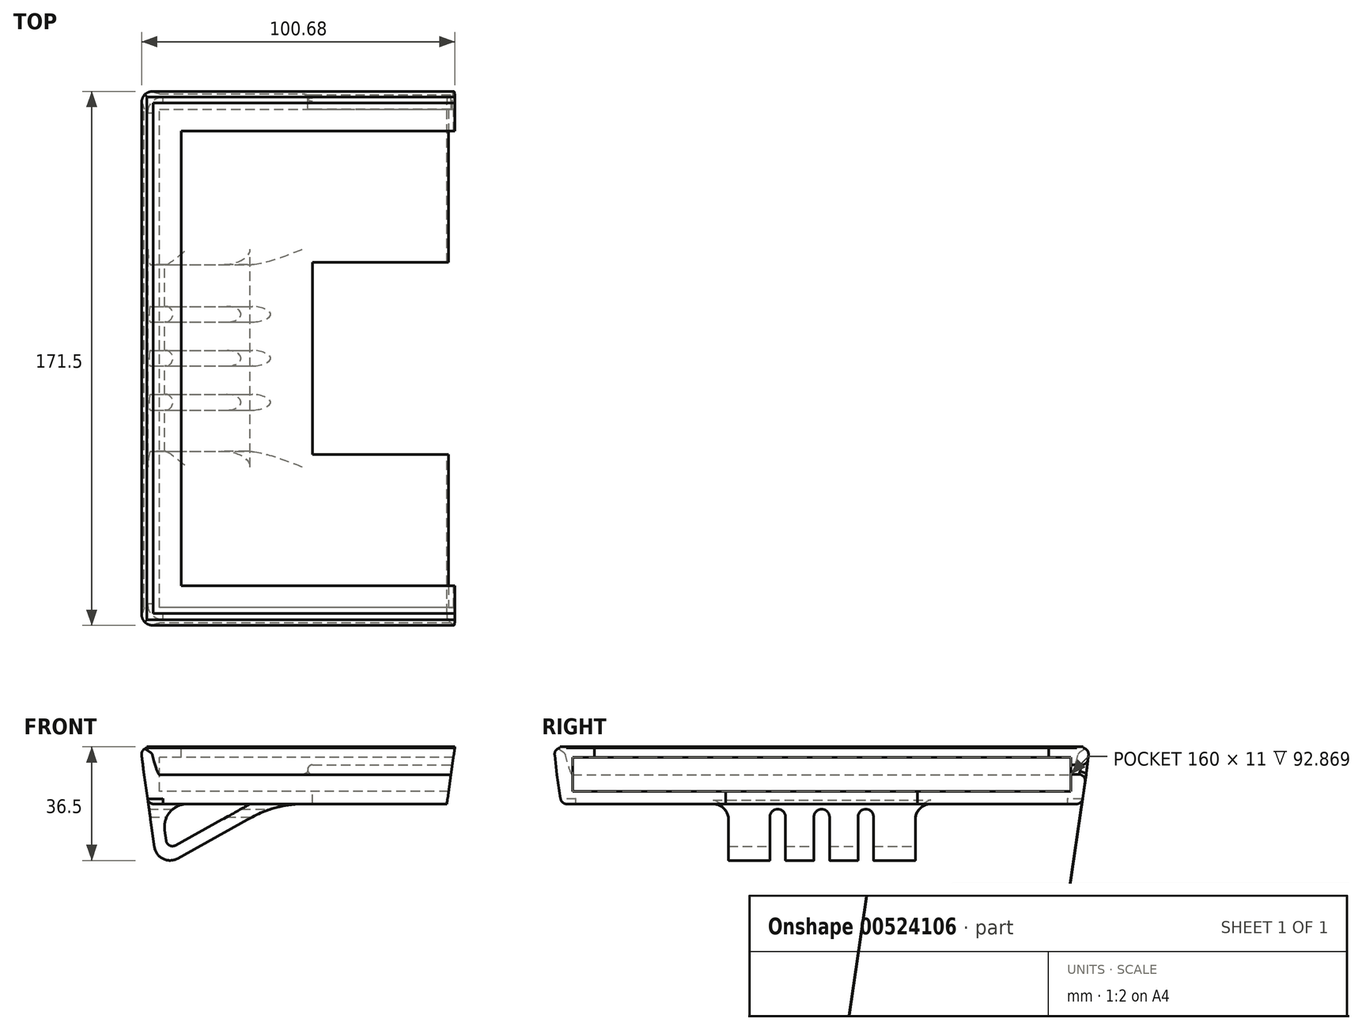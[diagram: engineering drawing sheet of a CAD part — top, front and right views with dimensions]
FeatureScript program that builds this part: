
annotation { "Feature Type Name" : "Feature", "Feature Type Description" : "" }
export const myFeature = defineFeature(function(context is Context, id is Id, definition is map)
    precondition{}
    {
        {
            var Q0;
            Q0=qCreatedBy(makeId("Right.planeOp"),FACE);
            var sketch = newSketch(context, id + "F0", { "sketchPlane" : qUnion([Q0])});
            skLineSegment(sketch, "E0.top", {"start": v(-5, -11) * mm, "end": v(44.17, -11) * mm});
            skLineSegment(sketch, "E0.right", {"start": v(44.17, -15) * mm, "end": v(44.17, -11) * mm});
            skLineSegment(sketch, "E1", {"start": v(2, 3) * mm, "end": v(2, 0) * mm});
            skLineSegment(sketch, "E2", {"start": v(2, 0) * mm, "end": v(-5, 0) * mm});
            skLineSegment(sketch, "E3", {"start": v(-5, 0) * mm, "end": v(-5, -11) * mm});
            skPoint(sketch, "E4.visualSharp", {"position": v(-11, 3) * mm});
            skPoint(sketch, "E5.visualSharp", {"position": v(-11, -15) * mm});
            skPoint(sketch, "E6.start.orphan", {"position": v(-9, -2) * mm});
            skPoint(sketch, "E7.end.orphan", {"position": v(-11, 1) * mm});
            skPoint(sketch, "E0.left.end.orphan", {"position": v(-11, -11) * mm});
            skPoint(sketch, "E5.filletArc.start.orphan", {"position": v(-11, -8) * mm});
            skLineSegment(sketch, "E8", {"start": v(-10.73, 0.76) * mm, "end": v(-9.97, -5.6) * mm});
            skPoint(sketch, "E9.orphan", {"position": v(-8.6, -7.27) * mm});
            skPoint(sketch, "E10.visualSharp", {"position": v(-9.77, -7.27) * mm});
            skArc(sketch, "E11.filletArc", {"start": v(-9, 2.99) * mm, "mid": v(-10.32, 2.23) * mm, "end": v(-10.73, 0.76) * mm});
            skLineSegment(sketch, "E12", {"start": v(44.17, -15) * mm, "end": v(-6.87, -15) * mm});
            skLineSegment(sketch, "E13", {"start": v(-9.97, -5.6) * mm, "end": v(-8.85, -13.29) * mm});
            skPoint(sketch, "E14.visualSharp", {"position": v(-8.6, -15) * mm});
            skArc(sketch, "E14.filletArc", {"start": v(-8.85, -13.29) * mm, "mid": v(-8.18, -14.51) * mm, "end": v(-6.87, -15) * mm});
            skLineSegment(sketch, "E15", {"start": v(-9, 2.99) * mm, "end": v(-9, 3.37) * mm});
            skLineSegment(sketch, "E16", {"start": v(-9, 3.37) * mm, "end": v(-6.98, 3.37) * mm});
            skLineSegment(sketch, "E17", {"start": v(-6.98, 3.37) * mm, "end": v(-6.98, 3) * mm});
            skPoint(sketch, "E18.start.orphan", {"position": v(-6.05, 3.37) * mm});
            skPoint(sketch, "E19.end.orphan", {"position": v(-6.05, 3) * mm});
            skLineSegment(sketch, "E20", {"start": v(-6.98, 3) * mm, "end": v(2, 3) * mm});
            skSolve(sketch);
        }
        {
            var Q0;
            Q0=qCreatedBy(makeId("Top.planeOp"),FACE);
            var sketch = newSketch(context, id + "F1", { "sketchPlane" : qUnion([Q0])});
            skLineSegment(sketch, "E21", {"start": v(0, 0) * mm, "end": v(-90, 0) * mm});
            skLineSegment(sketch, "E22", {"start": v(-90, 0) * mm, "end": v(-90, 150) * mm});
            skLineSegment(sketch, "E23", {"start": v(-90, 150) * mm, "end": v(0, 150) * mm});
            skSolve(sketch);
        }
        {
            var Q0;
            Q0 = qSketchRegion(id + "F0", true);
            var Q1;
            Q1=sQuery(id+"F1.wireOp",EDGE,"E21");
            var Q2;
            Q2=sQuery(id+"F1.wireOp",EDGE,"E22");
            var Q3;
            Q3=sQuery(id+"F1.wireOp",EDGE,"E23");
            sweep(context, id + "F2", {"profiles" : qUnion([Q0]), "path" : qUnion([Q1, Q2, Q3])});
        }
        {
            var Q0;
            Q0=makeQuery(id+"F2.opSweep","MID_CAP_EDGE",EDGE,{"disambiguationData":[OSD([sQuery(id+"F0.wireOp",EDGE,"E13"),sQuery(id+"F1.wireOp",VERTEX,"E22.start")])],"capPos":1.0});
            var Q1;
            Q1=makeQuery(id+"F2.opSweep","MID_CAP_EDGE",EDGE,{"disambiguationData":[OSD([sQuery(id+"F0.wireOp",EDGE,"E13"),sQuery(id+"F1.wireOp",VERTEX,"E23.start")])],"capPos":2.0});
            fillet(context, id + "F3", {"entities" : qUnion([Q0, Q1]), "radius" : 5 * mm, "tangentPropagation" : true, "allowEdgeOverflow" : false});
        }
        {
            var Q0;
            Q0=qCreatedBy(makeId("Front.planeOp"),FACE);
            cPlane(context, id + "F4", {"entities" : qUnion([Q0]), "cplaneType" : CPlaneType.OFFSET, "offset" : 162.7 * mm, "oppositeDirection" : true, "width" : 150 * mm, "height" : 150 * mm});
        }
        {
            var Q0;
            Q0=qCreatedBy(id+"F4.planeOp",FACE);
            var sketch = newSketch(context, id + "F5", { "sketchPlane" : qUnion([Q0])});
            skLineSegment(sketch, "E24", {"start": v(0, -2.44) * mm, "end": v(-45.86, -2.44) * mm});
            skLineSegment(sketch, "E25", {"start": v(-45.86, -5.5) * mm, "end": v(4.7, -5.5) * mm});
            skLineSegment(sketch, "E26", {"start": v(4.7, -5.5) * mm, "end": v(4.7, -2.44) * mm});
            skLineSegment(sketch, "E27", {"start": v(4.7, -2.44) * mm, "end": v(0, -2.44) * mm});
            skArc(sketch, "E28", {"start": v(-45.86, -2.44) * mm, "mid": v(-47.39, -3.97) * mm, "end": v(-45.86, -5.5) * mm});
            skSolve(sketch);
        }
        {
            var Q0;
            Q0 = qSketchRegion(id + "F5", true);
            extrude(context, id + "F6", {"entities" : qUnion([Q0]), "operationType" : NewBodyOperationType.REMOVE, "depth" : 10.7 * mm, "offsetDistance" : 25 * mm});
        }
        {
            var Q0;
            Q0=qCreatedBy(makeId("Front.planeOp"),FACE);
            cPlane(context, id + "F7", {"entities" : qUnion([Q0]), "cplaneType" : CPlaneType.OFFSET, "offset" : 75.1 * mm, "oppositeDirection" : true, "width" : 150 * mm, "height" : 150 * mm});
        }
        {
            var Q0;
            Q0=qCreatedBy(id+"F7.planeOp",FACE);
            var sketch = newSketch(context, id + "F8", { "sketchPlane" : qUnion([Q0])});
            skLineSegment(sketch, "E29", {"start": v(-100.25, -3.05) * mm, "end": v(-96.59, -28.83) * mm});
            skLineSegment(sketch, "E30", {"start": v(-89.21, -32.5) * mm, "end": v(-52.8, -12.34) * mm});
            skLineSegment(sketch, "E31.0", {"start": v(-89.88, -28.3) * mm, "end": v(-58.97, -11.2) * mm});
            skLineSegment(sketch, "E31.1", {"start": v(-96.3, -2.45) * mm, "end": v(-92.83, -26.83) * mm});
            skLineSegment(sketch, "E32", {"start": v(-58.97, -11.2) * mm, "end": v(-52.8, -12.34) * mm});
            skLineSegment(sketch, "E33", {"start": v(-96.3, -2.45) * mm, "end": v(-100.25, -3.05) * mm});
            skPoint(sketch, "E34.visualSharp", {"position": v(-92.42, -29.7) * mm});
            skArc(sketch, "E34.filletArc", {"start": v(-92.83, -26.83) * mm, "mid": v(-91.74, -28.34) * mm, "end": v(-89.88, -28.3) * mm});
            skPoint(sketch, "E35.visualSharp", {"position": v(-95.56, -36.02) * mm});
            skArc(sketch, "E35.filletArc", {"start": v(-96.59, -28.83) * mm, "mid": v(-93.86, -32.6) * mm, "end": v(-89.21, -32.5) * mm});
            skSolve(sketch);
        }
        {
            var Q0;
            Q0 = qSketchRegion(id + "F8", true);
            extrude(context, id + "F9", {"entities" : qUnion([Q0]), "operationType" : NewBodyOperationType.ADD, "endBound" : BoundingType.SYMMETRIC, "depth" : 60 * mm, "offsetDistance" : 25 * mm});
        }
        {
            var Q0;
            Q0=makeQuery(id+"F9.boolean.opBoolean","INTERSECT",EDGE,{"derivedFrom":[makeQuery(id+"F2.opSweep","SWEPT_FACE",FACE,{"disambiguationData":[OSD([sQuery(id+"F0.wireOp",EDGE,"E12"),sQuery(id+"F1.wireOp",EDGE,"E21")])]}),makeQuery(id+"F9.opExtrude","SWEPT_FACE",FACE,{"disambiguationData":[OSD([sQuery(id+"F8.wireOp",EDGE,"E30")])]})]});
            fillet(context, id + "F10", {"entities" : qUnion([Q0]), "radius" : 33.52 * mm, "tangentPropagation" : true, "allowEdgeOverflow" : false});
        }
        {
            var Q0;
            Q0=makeQuery(id+"F9.boolean.opBoolean","INTERSECT",EDGE,{"derivedFrom":[makeQuery(id+"F2.opSweep","SWEPT_FACE",FACE,{"disambiguationData":[OSD([sQuery(id+"F0.wireOp",EDGE,"E12"),sQuery(id+"F1.wireOp",EDGE,"E21")])]}),makeQuery(id+"F9.opExtrude","SWEPT_FACE",FACE,{"disambiguationData":[OSD([sQuery(id+"F8.wireOp",EDGE,"E31.1")])]})]});
            fillet(context, id + "F11", {"entities" : qUnion([Q0]), "radius" : 7.35 * mm, "tangentPropagation" : true, "allowEdgeOverflow" : false});
        }
        {
            var Q0;
            Q0=makeQuery(id+"F9.boolean.opBoolean","INTERSECT",EDGE,{"disambiguationData":[OD(1.0)],"derivedFrom":[makeQuery(id+"F2.opSweep","SWEPT_FACE",FACE,{"disambiguationData":[OSD([sQuery(id+"F0.wireOp",EDGE,"E12"),sQuery(id+"F1.wireOp",EDGE,"E21")])]}),makeQuery(id+"F9.opExtrude","CAP_FACE",FACE,{"disambiguationData":[OSD([sQuery(id+"F8.wireOp",EDGE,"E29"),sQuery(id+"F8.wireOp",EDGE,"E30"),sQuery(id+"F8.wireOp",EDGE,"E31.0"),sQuery(id+"F8.wireOp",EDGE,"E31.1"),sQuery(id+"F8.wireOp",EDGE,"E32"),sQuery(id+"F8.wireOp",EDGE,"E33"),sQuery(id+"F8.wireOp",EDGE,"E34.filletArc"),sQuery(id+"F8.wireOp",EDGE,"E35.filletArc")])],"isStart":false})]});
            var Q1;
            Q1=makeQuery(id+"F9.boolean.opBoolean","INTERSECT",EDGE,{"disambiguationData":[OD(1.0)],"derivedFrom":[makeQuery(id+"F2.opSweep","SWEPT_FACE",FACE,{"disambiguationData":[OSD([sQuery(id+"F0.wireOp",EDGE,"E12"),sQuery(id+"F1.wireOp",EDGE,"E21")])]}),makeQuery(id+"F9.opExtrude","CAP_FACE",FACE,{"disambiguationData":[OSD([sQuery(id+"F8.wireOp",EDGE,"E29"),sQuery(id+"F8.wireOp",EDGE,"E30"),sQuery(id+"F8.wireOp",EDGE,"E31.0"),sQuery(id+"F8.wireOp",EDGE,"E31.1"),sQuery(id+"F8.wireOp",EDGE,"E32"),sQuery(id+"F8.wireOp",EDGE,"E33"),sQuery(id+"F8.wireOp",EDGE,"E34.filletArc"),sQuery(id+"F8.wireOp",EDGE,"E35.filletArc")])],"isStart":true})]});
            var Q2;
            Q2=makeQuery(id+"F9.boolean.opBoolean","INTERSECT",EDGE,{"disambiguationData":[OD(0.0)],"derivedFrom":[makeQuery(id+"F2.opSweep","SWEPT_FACE",FACE,{"disambiguationData":[OSD([sQuery(id+"F0.wireOp",EDGE,"E12"),sQuery(id+"F1.wireOp",EDGE,"E21")])]}),makeQuery(id+"F9.opExtrude","CAP_FACE",FACE,{"disambiguationData":[OSD([sQuery(id+"F8.wireOp",EDGE,"E29"),sQuery(id+"F8.wireOp",EDGE,"E30"),sQuery(id+"F8.wireOp",EDGE,"E31.0"),sQuery(id+"F8.wireOp",EDGE,"E31.1"),sQuery(id+"F8.wireOp",EDGE,"E32"),sQuery(id+"F8.wireOp",EDGE,"E33"),sQuery(id+"F8.wireOp",EDGE,"E34.filletArc"),sQuery(id+"F8.wireOp",EDGE,"E35.filletArc")])],"isStart":false})]});
            var Q3;
            Q3=makeQuery(id+"F9.boolean.opBoolean","INTERSECT",EDGE,{"disambiguationData":[OD(0.0)],"derivedFrom":[makeQuery(id+"F2.opSweep","SWEPT_FACE",FACE,{"disambiguationData":[OSD([sQuery(id+"F0.wireOp",EDGE,"E12"),sQuery(id+"F1.wireOp",EDGE,"E21")])]}),makeQuery(id+"F9.opExtrude","CAP_FACE",FACE,{"disambiguationData":[OSD([sQuery(id+"F8.wireOp",EDGE,"E29"),sQuery(id+"F8.wireOp",EDGE,"E30"),sQuery(id+"F8.wireOp",EDGE,"E31.0"),sQuery(id+"F8.wireOp",EDGE,"E31.1"),sQuery(id+"F8.wireOp",EDGE,"E32"),sQuery(id+"F8.wireOp",EDGE,"E33"),sQuery(id+"F8.wireOp",EDGE,"E34.filletArc"),sQuery(id+"F8.wireOp",EDGE,"E35.filletArc")])],"isStart":true})]});
            fillet(context, id + "F12", {"entities" : qUnion([Q0, Q1, Q2, Q3]), "radius" : 5 * mm, "tangentPropagation" : true, "allowEdgeOverflow" : false});
        }
        {
            var Q0;
            Q0=qCreatedBy(makeId("Right.planeOp"),FACE);
            var sketch = newSketch(context, id + "F13", { "sketchPlane" : qUnion([Q0])});
            skLineSegment(sketch, "E36", {"start": v(75.04, -11.25) * mm, "end": v(75.04, -53.98) * mm, "construction": true});
            skLineSegment(sketch, "E37.left", {"start": v(75.04, -19.13) * mm, "end": v(75.04, -39.13) * mm, "construction": true});
            skArc(sketch, "E38", {"start": v(75.04, -16.63) * mm, "mid": v(73.27, -17.36) * mm, "end": v(72.54, -19.13) * mm});
            skArc(sketch, "E39", {"start": v(63.4, -19.15) * mm, "mid": v(60.87, -16.63) * mm, "end": v(58.4, -19.21) * mm});
            skLineSegment(sketch, "E40", {"start": v(58.4, -19.04) * mm, "end": v(58.4, -37.9) * mm});
            skLineSegment(sketch, "E41", {"start": v(58.4, -37.9) * mm, "end": v(60.37, -37.9) * mm});
            skLineSegment(sketch, "E42", {"start": v(63.4, -19.1) * mm, "end": v(63.4, -37.9) * mm});
            skLineSegment(sketch, "E43", {"start": v(63.4, -37.9) * mm, "end": v(60.37, -37.9) * mm});
            skPoint(sketch, "E37.top.end.orphan", {"position": v(72.54, -39.13) * mm});
            skLineSegment(sketch, "E44", {"start": v(72.54, -19.13) * mm, "end": v(72.54, -39.13) * mm});
            skLineSegment(sketch, "E45", {"start": v(75.04, -39.13) * mm, "end": v(72.54, -39.13) * mm});
            skArc(sketch, "E46.MirrorCS", {"start": v(75.04, -16.63) * mm, "mid": v(76.8, -17.36) * mm, "end": v(77.54, -19.13) * mm});
            skLineSegment(sketch, "E47.MirrorCS", {"start": v(77.54, -19.13) * mm, "end": v(77.54, -39.13) * mm});
            skLineSegment(sketch, "E48.MirrorCS", {"start": v(75.04, -39.13) * mm, "end": v(77.54, -39.13) * mm});
            skLineSegment(sketch, "E49.MirrorCS", {"start": v(86.68, -37.9) * mm, "end": v(89.7, -37.9) * mm});
            skLineSegment(sketch, "E50.MirrorCS", {"start": v(91.68, -37.9) * mm, "end": v(89.7, -37.9) * mm});
            skLineSegment(sketch, "E51.MirrorCS", {"start": v(91.68, -19.04) * mm, "end": v(91.68, -37.9) * mm});
            skLineSegment(sketch, "E52.MirrorCS", {"start": v(86.68, -19.1) * mm, "end": v(86.68, -37.9) * mm});
            skArc(sketch, "E53.MirrorCS", {"start": v(86.68, -19.15) * mm, "mid": v(89.2, -16.63) * mm, "end": v(91.68, -19.21) * mm});
            skSolve(sketch);
        }
        {
            var Q0;
            Q0 = qSketchRegion(id + "F13", true);
            extrude(context, id + "F14", {"entities" : qUnion([Q0]), "operationType" : NewBodyOperationType.REMOVE, "oppositeDirection" : true, "depth" : 100.9 * mm, "offsetDistance" : 25 * mm});
        }
        {
            var Q0;
            Q0=qCreatedBy(makeId("Front.planeOp"),FACE);
            var sketch = newSketch(context, id + "F15", { "sketchPlane" : qUnion([Q0])});
            skLineSegment(sketch, "E54", {"start": v(0, 3.83) * mm, "end": v(-3.19, -18.36) * mm});
            skLineSegment(sketch, "E55", {"start": v(-3.19, -18.36) * mm, "end": v(4.88, -18.36) * mm});
            skLineSegment(sketch, "E56", {"start": v(4.88, -18.36) * mm, "end": v(4.88, 6.8) * mm});
            skLineSegment(sketch, "E57", {"start": v(4.88, 6.8) * mm, "end": v(0, 6.8) * mm});
            skLineSegment(sketch, "E58", {"start": v(0, 6.8) * mm, "end": v(0, 3.83) * mm});
            skSolve(sketch);
        }
        {
            var Q0;
            Q0 = qSketchRegion(id + "F15", true);
            extrude(context, id + "F16", {"entities" : qUnion([Q0]), "operationType" : NewBodyOperationType.REMOVE, "endBound" : BoundingType.SYMMETRIC, "oppositeDirection" : true, "depth" : 342 * mm, "offsetDistance" : 25 * mm});
        }
        {
            var Q0;
            Q0=makeQuery(id+"F6.boolean.opBoolean","INTERSECT",EDGE,{"derivedFrom":[makeQuery(id+"F2.opSweep","SWEPT_FACE",FACE,{"disambiguationData":[OSD([sQuery(id+"F0.wireOp",EDGE,"E8"),sQuery(id+"F1.wireOp",EDGE,"E23")])]}),makeQuery(id+"F6.opExtrude","SWEPT_FACE",FACE,{"disambiguationData":[OSD([sQuery(id+"F5.wireOp",EDGE,"E24"),sQuery(id+"F5.wireOp",EDGE,"E27")])]})]});
            fillet(context, id + "F17", {"entities" : qUnion([Q0]), "radius" : 2 * mm, "tangentPropagation" : true, "allowEdgeOverflow" : false});
        }
    });
